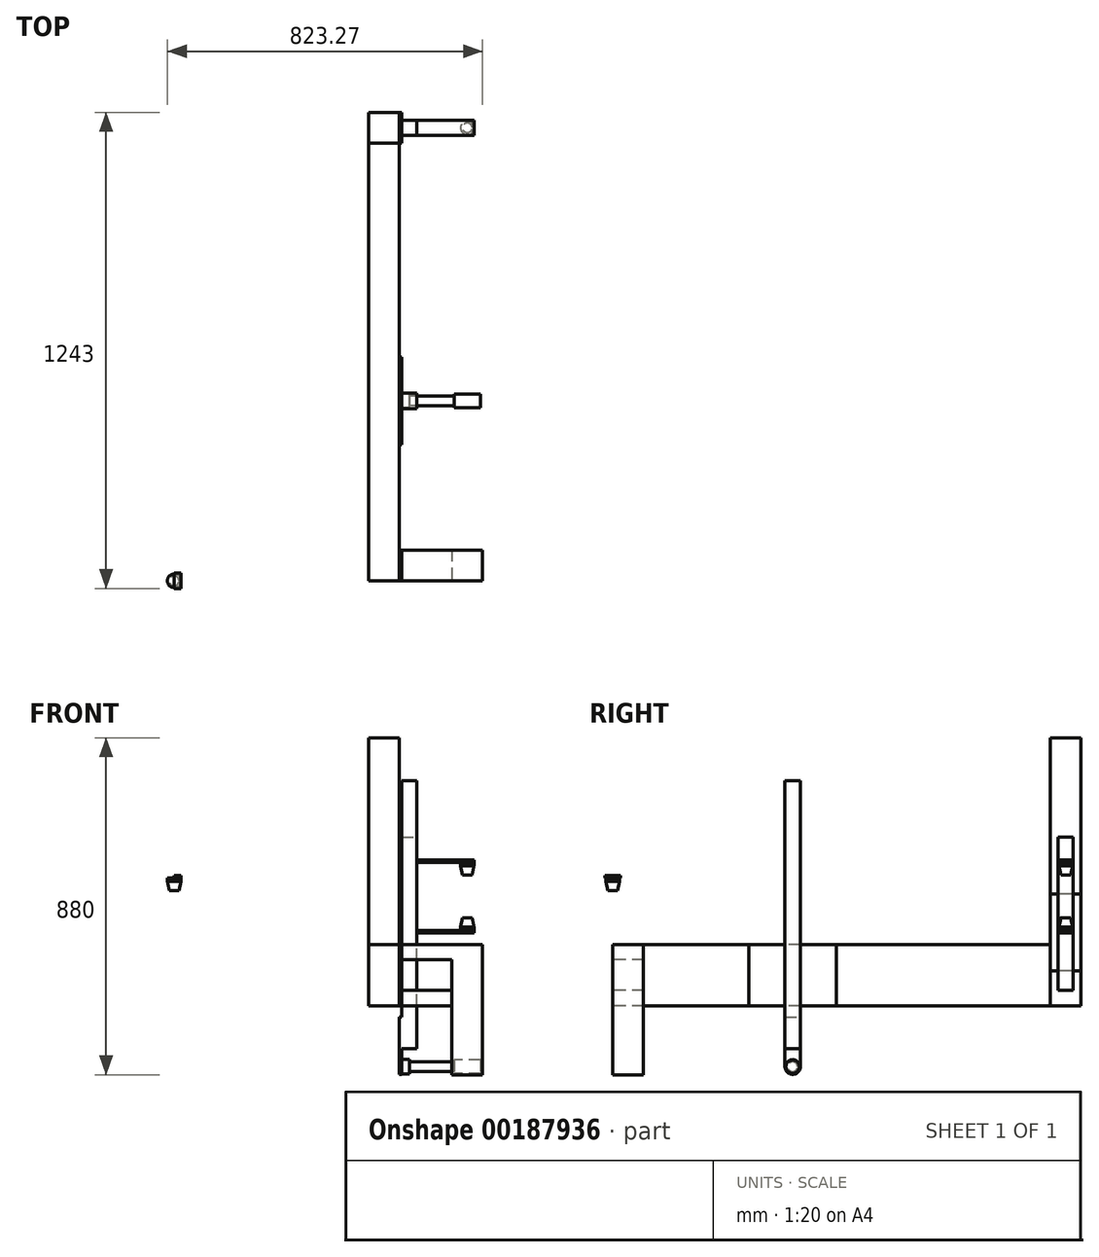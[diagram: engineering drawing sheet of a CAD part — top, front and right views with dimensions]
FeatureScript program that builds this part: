
annotation { "Feature Type Name" : "Feature", "Feature Type Description" : "" }
export const myFeature = defineFeature(function(context is Context, id is Id, definition is map)
    precondition{}
    {
        {
            var Q0;
            Q0=qCreatedBy(makeId("Front.planeOp"),FACE);
            var sketch = newSketch(context, id + "F0", { "sketchPlane" : qUnion([Q0])});
            skLineSegment(sketch, "E0", {"start": v(-374.77, -348.44) * mm, "end": v(-374.77, 351.56) * mm});
            skLineSegment(sketch, "E1", {"start": v(-334.77, -348.44) * mm, "end": v(-334.77, 351.56) * mm});
            skLineSegment(sketch, "E2", {"start": v(-334.77, 351.56) * mm, "end": v(-374.77, 351.56) * mm});
            skLineSegment(sketch, "E3", {"start": v(-334.77, -348.44) * mm, "end": v(-374.77, -348.44) * mm});
            skLineSegment(sketch, "E4", {"start": v(-374.77, -376.34) * mm, "end": v(-374.77, -413.47) * mm});
            skLineSegment(sketch, "E5", {"start": v(-374.77, -413.47) * mm, "end": v(-354.77, -413.47) * mm});
            skLineSegment(sketch, "E6", {"start": v(-354.77, -376.34) * mm, "end": v(-374.77, -376.34) * mm});
            skLineSegment(sketch, "E7", {"start": v(-381.12, -414.9) * mm, "end": v(-381.12, -264.9) * mm});
            skLineSegment(sketch, "E8", {"start": v(-381.12, -414.9) * mm, "end": v(-374.77, -414.9) * mm});
            skLineSegment(sketch, "E9", {"start": v(-374.77, -414.9) * mm, "end": v(-374.77, -264.9) * mm});
            skLineSegment(sketch, "E10", {"start": v(-374.77, -264.9) * mm, "end": v(-381.12, -264.9) * mm});
            skLineSegment(sketch, "E11.bottom", {"start": v(304.53, -11.1) * mm, "end": v(384.53, -11.1) * mm});
            skLineSegment(sketch, "E11.top", {"start": v(304.53, -171.1) * mm, "end": v(384.53, -171.1) * mm});
            skLineSegment(sketch, "E11.left", {"start": v(304.53, -11.1) * mm, "end": v(304.53, -171.1) * mm});
            skLineSegment(sketch, "E11.right", {"start": v(384.53, -11.1) * mm, "end": v(384.53, -171.1) * mm});
            skLineSegment(sketch, "E12", {"start": v(390.88, -11.1) * mm, "end": v(390.88, -171.1) * mm});
            skPoint(sketch, "E12.startSnap0", {"position": v(344.53, -11.1) * mm});
            skLineSegment(sketch, "E13", {"start": v(384.53, -11.1) * mm, "end": v(390.88, -11.1) * mm});
            skLineSegment(sketch, "E14", {"start": v(390.88, -11.1) * mm, "end": v(595.98, -11.1) * mm});
            skLineSegment(sketch, "E15", {"start": v(595.98, -11.1) * mm, "end": v(602.33, -11.1) * mm});
            skLineSegment(sketch, "E16", {"start": v(602.33, -11.1) * mm, "end": v(602.33, -51.1) * mm});
            skLineSegment(sketch, "E17", {"start": v(602.33, -51.1) * mm, "end": v(595.98, -51.1) * mm});
            skLineSegment(sketch, "E18", {"start": v(595.98, -51.1) * mm, "end": v(595.98, -11.1) * mm});
            skLineSegment(sketch, "E19", {"start": v(595.98, -51.1) * mm, "end": v(390.88, -51.1) * mm});
            skLineSegment(sketch, "E20", {"start": v(602.33, -51.1) * mm, "end": v(602.33, -351.1) * mm});
            skLineSegment(sketch, "E21", {"start": v(602.33, -351.1) * mm, "end": v(522.33, -351.1) * mm});
            skLineSegment(sketch, "E22", {"start": v(522.33, -351.1) * mm, "end": v(522.33, -51.1) * mm});
            skLineSegment(sketch, "E23", {"start": v(384.53, -171.1) * mm, "end": v(390.88, -171.1) * mm});
            skLineSegment(sketch, "E24", {"start": v(522.33, -171.1) * mm, "end": v(390.88, -171.1) * mm});
            skLineSegment(sketch, "E25", {"start": v(522.33, -171.1) * mm, "end": v(522.33, -131.1) * mm});
            skLineSegment(sketch, "E26", {"start": v(522.33, -131.1) * mm, "end": v(390.88, -131.1) * mm});
            skLineSegment(sketch, "E27", {"start": v(602.33, -222.88) * mm, "end": v(562.33, -222.88) * mm, "construction": true});
            skLineSegment(sketch, "E28", {"start": v(562.33, -222.88) * mm, "end": v(562.33, -101.4) * mm});
            skPoint(sketch, "E29", {"position": v(-381.12, -235.9) * mm});
            skLineSegment(sketch, "E30", {"start": v(-381.12, -235.9) * mm, "end": v(-381.12, -75.9) * mm});
            skLineSegment(sketch, "E31", {"start": v(-381.12, -75.9) * mm, "end": v(-374.77, -75.9) * mm});
            skLineSegment(sketch, "E32", {"start": v(-374.77, -75.9) * mm, "end": v(-374.77, -235.9) * mm});
            skLineSegment(sketch, "E33", {"start": v(-374.77, -235.9) * mm, "end": v(-381.12, -235.9) * mm});
            skLineSegment(sketch, "E34", {"start": v(-381.12, -394.9) * mm, "end": v(-203.32, -394.9) * mm});
            skLineSegment(sketch, "E35", {"start": v(-354.77, -376.34) * mm, "end": v(-354.77, -413.47) * mm});
            skLineSegment(sketch, "E36", {"start": v(-203.32, -394.9) * mm, "end": v(-203.32, 341.23) * mm});
            skLineSegment(sketch, "E37", {"start": v(-220.94, 162.85) * mm, "end": v(-203.32, 162.85) * mm});
            skLineSegment(sketch, "E38.MirrorCS", {"start": v(-185.7, 162.85) * mm, "end": v(-203.32, 162.85) * mm});
            skPoint(sketch, "E39", {"position": v(-203.32, 129.82) * mm});
            skPoint(sketch, "E40", {"position": v(-215.94, 129.82) * mm});
            skLineSegment(sketch, "E41", {"start": v(-220.94, 162.85) * mm, "end": v(-220.94, 153.82) * mm});
            skLineSegment(sketch, "E42", {"start": v(-220.94, 153.82) * mm, "end": v(-185.7, 153.82) * mm});
            skLineSegment(sketch, "E43", {"start": v(-185.7, 153.82) * mm, "end": v(-185.7, 162.85) * mm});
            skLineSegment(sketch, "E44", {"start": v(-220.94, 153.82) * mm, "end": v(-215.94, 129.82) * mm});
            skLineSegment(sketch, "E45", {"start": v(-203.32, 129.82) * mm, "end": v(-215.94, 129.82) * mm});
            skLineSegment(sketch, "E46.MirrorCS", {"start": v(-185.7, 153.82) * mm, "end": v(-190.7, 129.82) * mm});
            skLineSegment(sketch, "E47.MirrorCS", {"start": v(-203.32, 129.82) * mm, "end": v(-190.7, 129.82) * mm});
            skLineSegment(sketch, "E48", {"start": v(-185.7, 162.85) * mm, "end": v(-185.7, 169.2) * mm});
            skLineSegment(sketch, "E49", {"start": v(-185.7, 169.2) * mm, "end": v(-334.77, 169.2) * mm});
            skLineSegment(sketch, "E50", {"start": v(-334.77, 169.2) * mm, "end": v(-334.77, 162.85) * mm});
            skLineSegment(sketch, "E51", {"start": v(-334.77, 162.85) * mm, "end": v(-185.7, 162.85) * mm});
            skPoint(sketch, "E52", {"position": v(-237.32, -377.4) * mm});
            skLineSegment(sketch, "E53", {"start": v(-237.32, -377.4) * mm, "end": v(-203.32, -377.4) * mm});
            skLineSegment(sketch, "E54", {"start": v(-237.32, -377.4) * mm, "end": v(-237.32, -394.9) * mm});
            skLineSegment(sketch, "E55.MirrorCS", {"start": v(-237.32, -412.4) * mm, "end": v(-203.32, -412.4) * mm});
            skLineSegment(sketch, "E56.MirrorCS", {"start": v(-237.32, -412.4) * mm, "end": v(-237.32, -394.9) * mm});
            skLineSegment(sketch, "E57.MirrorCS", {"start": v(-169.32, -377.4) * mm, "end": v(-203.32, -377.4) * mm});
            skLineSegment(sketch, "E58.MirrorCS", {"start": v(-169.32, -377.4) * mm, "end": v(-169.32, -394.9) * mm});
            skLineSegment(sketch, "E59.MirrorCS", {"start": v(-25.52, -394.9) * mm, "end": v(-203.32, -394.9) * mm});
            skLineSegment(sketch, "E60.MirrorCS", {"start": v(-169.32, -412.4) * mm, "end": v(-203.32, -412.4) * mm});
            skLineSegment(sketch, "E61.MirrorCS", {"start": v(-169.32, -412.4) * mm, "end": v(-169.32, -394.9) * mm});
            skPoint(sketch, "E62", {"position": v(-354.77, -382.2) * mm});
            skPoint(sketch, "E63", {"position": v(-354.77, -394.9) * mm});
            skLineSegment(sketch, "E64", {"start": v(-354.77, -382.2) * mm, "end": v(-237.32, -382.2) * mm});
            skLineSegment(sketch, "E65.MirrorCS", {"start": v(-354.77, -407.6) * mm, "end": v(-237.32, -407.6) * mm});
            skPoint(sketch, "E66", {"position": v(-374.77, -394.9) * mm});
            skLineSegment(sketch, "E67", {"start": v(1447.18, -161.35) * mm, "end": v(1447.18, 38.65) * mm});
            skLineSegment(sketch, "E68", {"start": v(1447.18, 38.65) * mm, "end": v(1527.18, 38.65) * mm});
            skLineSegment(sketch, "E69", {"start": v(1527.18, 38.65) * mm, "end": v(1527.18, -161.35) * mm});
            skLineSegment(sketch, "E70", {"start": v(1447.18, -161.35) * mm, "end": v(1527.18, -161.35) * mm});
            skCircle(sketch, "E71", {"center": v(1507.18, 18.65) * mm, "radius": 4 * mm});
            skCircle(sketch, "E72", {"center": v(1467.18, -141.35) * mm, "radius": 4 * mm});
            skLineSegment(sketch, "E73", {"start": v(1496.49, 18.47) * mm, "end": v(1494.06, 30.94) * mm});
            skLineSegment(sketch, "E74", {"start": v(1493.7, 18.25) * mm, "end": v(1491.06, 30.68) * mm});
            skLineSegment(sketch, "E75", {"start": v(1490.91, 18) * mm, "end": v(1488.06, 30.38) * mm});
            skLineSegment(sketch, "E76", {"start": v(1488.14, 17.69) * mm, "end": v(1485.06, 30.02) * mm});
            skLineSegment(sketch, "E77", {"start": v(1486.65, 12.52) * mm, "end": v(1482.05, 29.7) * mm});
            skLineSegment(sketch, "E78", {"start": v(1482.6, 16.93) * mm, "end": v(1479.1, 29.14) * mm});
            skLineSegment(sketch, "E79", {"start": v(1479.84, 16.47) * mm, "end": v(1476.12, 28.62) * mm});
            skLineSegment(sketch, "E80", {"start": v(1477.09, 15.97) * mm, "end": v(1473.16, 28.06) * mm});
            skLineSegment(sketch, "E81", {"start": v(1474.35, 15.42) * mm, "end": v(1470.21, 27.44) * mm});
            skLineSegment(sketch, "E82", {"start": v(1473.32, 10.15) * mm, "end": v(1467.24, 26.85) * mm});
            skLineSegment(sketch, "E83", {"start": v(1468.9, 14.18) * mm, "end": v(1464.34, 26.04) * mm});
            skLineSegment(sketch, "E84", {"start": v(1466.19, 13.49) * mm, "end": v(1461.43, 25.27) * mm});
            skLineSegment(sketch, "E85", {"start": v(1463.5, 12.75) * mm, "end": v(1458.53, 24.45) * mm});
            skLineSegment(sketch, "E86", {"start": v(1460.81, 11.96) * mm, "end": v(1455.64, 23.57) * mm});
            skLineSegment(sketch, "E87", {"start": v(1460.25, 6.62) * mm, "end": v(1452.73, 22.73) * mm});
            skCircle(sketch, "E88", {"center": v(1518.58, -38.02) * mm, "radius": 3.37 * mm});
            skCircle(sketch, "E89", {"center": v(1507.18, -141.35) * mm, "radius": 4 * mm});
            skCircle(sketch, "E90", {"center": v(1507.18, 3.65) * mm, "radius": 3.96 * mm});
            skCircle(sketch, "E91", {"center": v(1467.18, -126.35) * mm, "radius": 3.96 * mm});
            skCircle(sketch, "E92", {"center": v(1507.18, -126.35) * mm, "radius": 3.96 * mm});
            skLineSegment(sketch, "E93", {"start": v(1416.45, 134) * mm, "end": v(1403.21, 209.03) * mm});
            skLineSegment(sketch, "E94", {"start": v(1403.21, 209.03) * mm, "end": v(1445.73, 216.53) * mm});
            skLineSegment(sketch, "E95", {"start": v(1416.45, 134) * mm, "end": v(1458.96, 141.49) * mm});
            skLineSegment(sketch, "E96", {"start": v(1445.73, 216.53) * mm, "end": v(1458.96, 141.49) * mm});
            skArc(sketch, "E97", {"start": v(1442.98, 167.35) * mm, "mid": v(1430.51, 171.3) * mm, "end": v(1417.64, 173.58) * mm});
            skArc(sketch, "E98", {"start": v(1445.88, 174.8) * mm, "mid": v(1432.42, 179.06) * mm, "end": v(1418.52, 181.53) * mm});
            skArc(sketch, "E99", {"start": v(1418.52, 181.53) * mm, "mid": v(1414.1, 178) * mm, "end": v(1417.64, 173.58) * mm});
            skArc(sketch, "E100", {"start": v(1442.98, 167.35) * mm, "mid": v(1448.16, 169.63) * mm, "end": v(1445.88, 174.8) * mm});
            skLineSegment(sketch, "E101.bottom", {"start": v(897.87, 19.19) * mm, "end": v(904.22, 19.19) * mm});
            skLineSegment(sketch, "E101.top", {"start": v(897.87, -180.81) * mm, "end": v(904.22, -180.81) * mm});
            skLineSegment(sketch, "E101.left", {"start": v(897.87, 19.19) * mm, "end": v(897.87, -180.81) * mm});
            skLineSegment(sketch, "E101.right", {"start": v(904.22, 19.19) * mm, "end": v(904.22, -180.81) * mm});
            skLineSegment(sketch, "E102", {"start": v(944.22, -232.06) * mm, "end": v(944.22, 167.94) * mm});
            skLineSegment(sketch, "E103", {"start": v(904.22, 19.19) * mm, "end": v(904.22, 167.94) * mm});
            skLineSegment(sketch, "E104", {"start": v(904.22, 167.94) * mm, "end": v(944.22, 167.94) * mm});
            skLineSegment(sketch, "E105", {"start": v(904.22, -180.81) * mm, "end": v(904.22, -232.06) * mm});
            skLineSegment(sketch, "E106", {"start": v(904.22, -232.06) * mm, "end": v(944.22, -232.06) * mm});
            skLineSegment(sketch, "E107", {"start": v(1075.67, 222.27) * mm, "end": v(1075.67, -239.92) * mm, "construction": true});
            skLineSegment(sketch, "E108", {"start": v(842.92, 393.35) * mm, "end": v(842.92, 384.33) * mm});
            skLineSegment(sketch, "E109", {"start": v(842.92, 384.33) * mm, "end": v(878.17, 384.33) * mm});
            skLineSegment(sketch, "E110", {"start": v(878.17, 384.33) * mm, "end": v(878.17, 393.35) * mm});
            skLineSegment(sketch, "E111", {"start": v(842.92, 384.33) * mm, "end": v(847.92, 360.33) * mm});
            skLineSegment(sketch, "E112", {"start": v(860.54, 360.33) * mm, "end": v(847.92, 360.33) * mm});
            skLineSegment(sketch, "E113.MirrorCS", {"start": v(878.17, 384.33) * mm, "end": v(873.17, 360.33) * mm});
            skLineSegment(sketch, "E114.MirrorCS", {"start": v(860.54, 360.33) * mm, "end": v(873.17, 360.33) * mm});
            skLineSegment(sketch, "E115", {"start": v(2139.53, 452.77) * mm, "end": v(2139.53, -9.42) * mm, "construction": true});
            skLineSegment(sketch, "E116", {"start": v(860.54, 360.33) * mm, "end": v(860.54, 393.35) * mm});
            skLineSegment(sketch, "E117", {"start": v(1075.67, 123.78) * mm, "end": v(1093.3, 123.78) * mm, "construction": true});
            skLineSegment(sketch, "E118", {"start": v(944.22, 109.05) * mm, "end": v(1093.3, 109.05) * mm});
            skLineSegment(sketch, "E119", {"start": v(1093.3, 109.05) * mm, "end": v(1093.3, 102.7) * mm});
            skLineSegment(sketch, "E120", {"start": v(1093.3, 102.7) * mm, "end": v(944.22, 102.7) * mm});
            skLineSegment(sketch, "E121.MirrorCS", {"start": v(1075.67, 123.78) * mm, "end": v(1058.05, 123.78) * mm, "construction": true});
            skLineSegment(sketch, "E122", {"start": v(1058.05, 102.7) * mm, "end": v(1058.05, 93.8) * mm});
            skLineSegment(sketch, "E123", {"start": v(1058.05, 93.8) * mm, "end": v(1075.67, 93.8) * mm});
            skLineSegment(sketch, "E124.MirrorCS", {"start": v(1075.67, 69.68) * mm, "end": v(1063.05, 69.68) * mm});
            skLineSegment(sketch, "E125", {"start": v(1058.05, 93.8) * mm, "end": v(1063.05, 69.68) * mm});
            skPoint(sketch, "E126", {"position": v(1075.67, 13.8) * mm});
            skLineSegment(sketch, "E127", {"start": v(1060.15, 13.8) * mm, "end": v(1101.33, 13.8) * mm, "construction": true});
            skLineSegment(sketch, "E128.MirrorCS", {"start": v(944.22, -81.43) * mm, "end": v(1093.3, -81.43) * mm});
            skLineSegment(sketch, "E129.MirrorCS", {"start": v(1093.3, -75.08) * mm, "end": v(944.22, -75.08) * mm});
            skLineSegment(sketch, "E130.MirrorCS", {"start": v(1075.67, -42.06) * mm, "end": v(1063.05, -42.06) * mm});
            skLineSegment(sketch, "E131.MirrorCS", {"start": v(1058.05, -66.2) * mm, "end": v(1063.05, -42.06) * mm});
            skLineSegment(sketch, "E132.MirrorCS", {"start": v(1058.05, -75.08) * mm, "end": v(1058.05, -66.2) * mm});
            skLineSegment(sketch, "E133.MirrorCS", {"start": v(1093.3, -81.43) * mm, "end": v(1093.3, -75.08) * mm});
            skLineSegment(sketch, "E134", {"start": v(1075.67, 102.7) * mm, "end": v(1075.67, 69.68) * mm});
            skLineSegment(sketch, "E135", {"start": v(1075.67, -42.06) * mm, "end": v(1075.67, -75.08) * mm});
            skPoint(sketch, "E136.orphan", {"position": v(1093.3, 93.8) * mm});
            skLineSegment(sketch, "E137", {"start": v(1058.05, -66.2) * mm, "end": v(1075.67, -66.2) * mm});
            skSolve(sketch);
        }
        {
            var Q0;
            Q0=makeQuery(id+"F0.imprint","IMPRINT",FACE,{"disambiguationData":[TD([[makeQuery(id+"F0.imprint","IMPRINT",EDGE,{"derivedFrom":sQuery(id+"F0.wireOp",EDGE,"E11.bottom")}),-1.0]])]});
            extrude(context, id + "F1", {"entities" : qUnion([Q0]), "oppositeDirection" : true, "depth" : 1143 * mm});
        }
        {
            var Q0;
            {var subQ3=sQuery(id+"F0.wireOp",EDGE,"E14");Q0=makeQuery(id+"F0.imprint","IMPRINT",FACE,{"disambiguationData":[TD([[makeQuery(id+"F0.imprint","IMPRINT",EDGE,{"derivedFrom":subQ3}),-1.0]])]});}
            extrude(context, id + "F2", {"entities" : qUnion([Q0]), "oppositeDirection" : true, "depth" : 80 * mm});
        }
        {
            var Q0;
            {var subQ1=sQuery(id+"F0.wireOp",EDGE,"E17");Q0=makeQuery(id+"F0.imprint","IMPRINT",FACE,{"disambiguationData":[TD([[makeQuery(id+"F0.imprint","IMPRINT",EDGE,{"derivedFrom":subQ1}),1.0]])]});}
            extrude(context, id + "F3", {"entities" : qUnion([Q0]), "operationType" : NewBodyOperationType.ADD, "oppositeDirection" : true, "depth" : 80 * mm});
        }
        {
            var Q0;
            Q0=makeQuery(id+"F0.imprint","IMPRINT",FACE,{"disambiguationData":[TD([[makeQuery(id+"F0.imprint","IMPRINT",EDGE,{"derivedFrom":sQuery(id+"F0.wireOp",EDGE,"E15")}),-1.0]])]});
            extrude(context, id + "F4", {"entities" : qUnion([Q0]), "operationType" : NewBodyOperationType.ADD, "oppositeDirection" : true, "depth" : 80 * mm});
        }
        {
            var Q0;
            Q0=makeQuery(id+"F0.imprint","IMPRINT",FACE,{"disambiguationData":[TD([[makeQuery(id+"F0.imprint","IMPRINT",EDGE,{"derivedFrom":sQuery(id+"F0.wireOp",EDGE,"E11.right")}),1.0]])]});
            extrude(context, id + "F5", {"entities" : qUnion([Q0]), "oppositeDirection" : true, "depth" : 80 * mm});
        }
        {
            var Q0;
            Q0=makeQuery(id+"F1.opExtrude","SWEPT_FACE",FACE,{"disambiguationData":[OSD([sQuery(id+"F0.wireOp",EDGE,"E11.right")])]});
            extrude(context, id + "F6", {"entities" : qUnion([Q0]), "oppositeDirection" : true, "depth" : 80 * mm});
        }
        {
            var Q0;
            Q0=makeQuery(id+"F1.opExtrude","CAP_FACE",FACE,{"disambiguationData":[OSD([sQuery(id+"F0.wireOp",EDGE,"E11.bottom"),sQuery(id+"F0.wireOp",EDGE,"E11.top"),sQuery(id+"F0.wireOp",EDGE,"E11.left"),sQuery(id+"F0.wireOp",EDGE,"E11.right")])],"isStart":false});
            var sketch = newSketch(context, id + "F7", { "sketchPlane" : qUnion([Q0])});
            skLineSegment(sketch, "E138.bottom", {"start": v(-384.53, -171.1) * mm, "end": v(-304.53, -171.1) * mm});
            skLineSegment(sketch, "E138.top", {"start": v(-384.53, -171.1) * mm, "end": v(-304.53, -171.1) * mm});
            skLineSegment(sketch, "E138.left", {"start": v(-384.53, -171.1) * mm, "end": v(-384.53, -171.1) * mm});
            skLineSegment(sketch, "E138.right", {"start": v(-304.53, -171.1) * mm, "end": v(-304.53, -171.1) * mm});
            skLineSegment(sketch, "E139.bottom", {"start": v(-304.53, 528.9) * mm, "end": v(-384.53, 528.9) * mm});
            skLineSegment(sketch, "E139.top", {"start": v(-304.53, -171.1) * mm, "end": v(-384.53, -171.1) * mm});
            skLineSegment(sketch, "E139.left", {"start": v(-304.53, 528.9) * mm, "end": v(-304.53, -171.1) * mm});
            skLineSegment(sketch, "E139.right", {"start": v(-384.53, 528.9) * mm, "end": v(-384.53, -171.1) * mm});
            skSolve(sketch);
        }
        {
            var Q0;
            Q0 = qSketchRegion(id + "F7", true);
            extrude(context, id + "F8", {"entities" : qUnion([Q0]), "depth" : 80 * mm});
        }
        {
            var Q0;
            {var subQ0=sQuery(id+"F0.wireOp",EDGE,"E24");Q0=makeQuery(id+"F0.imprint","IMPRINT",FACE,{"disambiguationData":[TD([[makeQuery(id+"F0.imprint","IMPRINT",EDGE,{"derivedFrom":subQ0}),-1.0]])]});}
            extrude(context, id + "F9", {"entities" : qUnion([Q0]), "oppositeDirection" : true, "depth" : 80 * mm});
        }
        {
            var Q0;
            {var subQ0=sQuery(id+"F0.wireOp",EDGE,"E2");Q0=makeQuery(id+"F0.imprint","IMPRINT",FACE,{"disambiguationData":[TD([[makeQuery(id+"F0.imprint","IMPRINT",EDGE,{"derivedFrom":subQ0}),1.0]])]});}
            var Q1;
            Q1=sQuery(id+"F0.wireOp",EDGE,"E34");
            var Q2;
            Q2=sQuery(id+"F0.wireOp",EDGE,"E59.MirrorCS");
            extrude(context, id + "F10", {"entities" : qUnion([Q0]), "surfaceEntities" : qUnion([Q1, Q2]), "endBound" : BoundingType.SYMMETRIC, "oppositeDirection" : true, "depth" : 40 * mm});
        }
        {
            var Q0;
            {var subQ5=sQuery(id+"F0.wireOp",EDGE,"E64");Q0=makeQuery(id+"F0.imprint","IMPRINT",FACE,{"disambiguationData":[TD([[makeQuery(id+"F0.imprint","IMPRINT",EDGE,{"derivedFrom":subQ5}),-1.0]])]});}
            var Q1;
            Q1=sQuery(id+"F0.wireOp",EDGE,"E34");
            revolve(context, id + "F11", {"entities" : qUnion([Q0]), "axis" : qUnion([Q1]), "revolveType" : RevolveType.FULL});
        }
        {
            var Q0;
            Q0=makeQuery(id+"F0.imprint","IMPRINT",FACE,{"disambiguationData":[TD([[makeQuery(id+"F0.imprint","IMPRINT",EDGE,{"derivedFrom":sQuery(id+"F0.wireOp",EDGE,"E30")}),-1.0]])]});
            extrude(context, id + "F12", {"entities" : qUnion([Q0]), "operationType" : NewBodyOperationType.ADD, "endBound" : BoundingType.SYMMETRIC, "oppositeDirection" : true, "depth" : 228.6 * mm});
        }
        {
            var Q0;
            {var subQ7=sQuery(id+"F0.wireOp",EDGE,"E10");Q0=makeQuery(id+"F0.imprint","IMPRINT",FACE,{"disambiguationData":[TD([[makeQuery(id+"F0.imprint","IMPRINT",EDGE,{"derivedFrom":subQ7}),1.0]])]});}
            var Q1;
            {var subQ4=sQuery(id+"F0.wireOp",EDGE,"E8");Q1=makeQuery(id+"F0.imprint","IMPRINT",FACE,{"disambiguationData":[TD([[makeQuery(id+"F0.imprint","IMPRINT",EDGE,{"derivedFrom":subQ4}),1.0]])]});}
            extrude(context, id + "F13", {"entities" : qUnion([Q0, Q1]), "operationType" : NewBodyOperationType.ADD, "endBound" : BoundingType.SYMMETRIC, "depth" : 40 * mm});
        }
        {
            var Q0;
            Q0=makeQuery(id+"F13.opExtrude","CAP_EDGE",EDGE,{"disambiguationData":[OSD([sQuery(id+"F0.wireOp",EDGE,"E8")])],"isStart":false});
            var Q1;
            Q1=makeQuery(id+"F13.opExtrude","CAP_EDGE",EDGE,{"disambiguationData":[OSD([sQuery(id+"F0.wireOp",EDGE,"E8")])],"isStart":true});
            fillet(context, id + "F14", {"entities" : qUnion([Q0, Q1]), "radius" : 20 * mm, "tangentPropagation" : true, "allowEdgeOverflow" : false});
        }
        {
            var Q0;
            {var subQ5=sQuery(id+"F0.wireOp",EDGE,"E6");Q0=makeQuery(id+"F0.imprint","IMPRINT",FACE,{"disambiguationData":[TD([[makeQuery(id+"F0.imprint","IMPRINT",EDGE,{"derivedFrom":subQ5}),1.0]])]});}
            var Q1;
            Q1=sQuery(id+"F0.wireOp",EDGE,"E34");
            revolve(context, id + "F15", {"entities" : qUnion([Q0]), "axis" : qUnion([Q1]), "revolveType" : RevolveType.FULL});
        }
        {
            var Q0;
            {var subQ1=sQuery(id+"F0.wireOp",EDGE,"E53");Q0=makeQuery(id+"F0.imprint","IMPRINT",FACE,{"disambiguationData":[TD([[makeQuery(id+"F0.imprint","IMPRINT",EDGE,{"derivedFrom":subQ1}),-1.0]])]});}
            var Q1;
            {var subQ3=sQuery(id+"F0.wireOp",EDGE,"E57.MirrorCS");Q1=makeQuery(id+"F0.imprint","IMPRINT",FACE,{"disambiguationData":[TD([[makeQuery(id+"F0.imprint","IMPRINT",EDGE,{"derivedFrom":subQ3}),1.0]])]});}
            var Q2;
            Q2=sQuery(id+"F0.wireOp",EDGE,"E53");
            var Q3;
            Q3=sQuery(id+"F0.wireOp",EDGE,"E57.MirrorCS");
            var Q4;
            Q4=sQuery(id+"F0.wireOp",EDGE,"E34");
            revolve(context, id + "F16", {"operationType" : NewBodyOperationType.ADD, "entities" : qUnion([Q0, Q1]), "surfaceEntities" : qUnion([Q2, Q3]), "axis" : qUnion([Q4]), "revolveType" : RevolveType.FULL});
        }
        {
            var Q0;
            {var subQ2=sQuery(id+"F0.wireOp",EDGE,"E50");Q0=makeQuery(id+"F0.imprint","IMPRINT",FACE,{"disambiguationData":[TD([[makeQuery(id+"F0.imprint","IMPRINT",EDGE,{"derivedFrom":subQ2}),1.0]])]});}
            var Q1;
            {var subQ5=sQuery(id+"F0.wireOp",EDGE,"E48");Q1=makeQuery(id+"F0.imprint","IMPRINT",FACE,{"disambiguationData":[TD([[makeQuery(id+"F0.imprint","IMPRINT",EDGE,{"derivedFrom":subQ5}),1.0]])]});}
            var Q2;
            Q2=sQuery(id+"F0.wireOp",EDGE,"E49");
            extrude(context, id + "F17", {"entities" : qUnion([Q0, Q1]), "operationType" : NewBodyOperationType.ADD, "surfaceEntities" : qUnion([Q2]), "endBound" : BoundingType.SYMMETRIC, "depth" : 40 * mm});
        }
        {
            var Q0;
            {var subQ5=sQuery(id+"F0.wireOp",EDGE,"E41");Q0=makeQuery(id+"F0.imprint","IMPRINT",FACE,{"disambiguationData":[TD([[makeQuery(id+"F0.imprint","IMPRINT",EDGE,{"derivedFrom":subQ5}),1.0]])]});}
            var Q1;
            {var subQ4=sQuery(id+"F0.wireOp",EDGE,"E44");Q1=makeQuery(id+"F0.imprint","IMPRINT",FACE,{"disambiguationData":[TD([[makeQuery(id+"F0.imprint","IMPRINT",EDGE,{"derivedFrom":subQ4}),1.0]])]});}
            var Q2;
            Q2=sQuery(id+"F0.wireOp",EDGE,"E36");
            revolve(context, id + "F18", {"operationType" : NewBodyOperationType.ADD, "entities" : qUnion([Q0, Q1]), "axis" : qUnion([Q2]), "revolveType" : RevolveType.FULL});
        }
        {
            var Q0;
            Q0=makeQuery(id+"F15.opRevolve","SWEPT_BODY",BODY,{"disambiguationData":[OSD([sQuery(id+"F0.wireOp",EDGE,"E6"),sQuery(id+"F0.wireOp",EDGE,"E9"),sQuery(id+"F0.wireOp",EDGE,"E34"),sQuery(id+"F0.wireOp",EDGE,"E35")])]});
            var Q1;
            Q1=makeQuery(id+"F10.opExtrude","SWEPT_BODY",BODY,{"disambiguationData":[OSD([sQuery(id+"F0.wireOp",EDGE,"E0"),sQuery(id+"F0.wireOp",EDGE,"E1"),sQuery(id+"F0.wireOp",EDGE,"E2"),sQuery(id+"F0.wireOp",EDGE,"E3"),sQuery(id+"F0.wireOp",EDGE,"E9"),sQuery(id+"F0.wireOp",EDGE,"E32"),sQuery(id+"F0.wireOp",EDGE,"E50")])]});
            var Q2;
            Q2=makeQuery(id+"F11.opRevolve","SWEPT_BODY",BODY,{"disambiguationData":[OSD([sQuery(id+"F0.wireOp",EDGE,"E34"),sQuery(id+"F0.wireOp",EDGE,"E35"),sQuery(id+"F0.wireOp",EDGE,"E54"),sQuery(id+"F0.wireOp",EDGE,"E64")])]});
            var Q3;
            Q3=makeQuery(id+"F12.opExtrude","CAP_VERTEX",VERTEX,{"disambiguationData":[OSD([sQuery(id+"F0.wireOp",EDGE,"E30"),sQuery(id+"F0.wireOp",EDGE,"E31")])],"isStart":false});
            var Q4;
            Q4=makeQuery(id+"F1.opExtrude","CAP_VERTEX",VERTEX,{"disambiguationData":[OSD([sQuery(id+"F0.wireOp",EDGE,"E11.bottom"),sQuery(id+"F0.wireOp",EDGE,"E11.right"),sQuery(id+"F0.wireOp",EDGE,"E13")])],"isStart":false});
            transform(context, id + "F19", {"entities" : qUnion([Q0, Q1, Q2]), "transformType" : TransformType.TRANSLATION_ENTITY, "oppositeDirectionEntity" : false, "transformLine" : qUnion([Q3, Q4]), "makeCopy" : false});
        }
        {
            var Q0;
            Q0=makeQuery(id+"F10.opExtrude","SWEPT_BODY",BODY,{"disambiguationData":[OSD([sQuery(id+"F0.wireOp",EDGE,"E0"),sQuery(id+"F0.wireOp",EDGE,"E1"),sQuery(id+"F0.wireOp",EDGE,"E2"),sQuery(id+"F0.wireOp",EDGE,"E3"),sQuery(id+"F0.wireOp",EDGE,"E9"),sQuery(id+"F0.wireOp",EDGE,"E32"),sQuery(id+"F0.wireOp",EDGE,"E50")])]});
            var Q1;
            Q1=makeQuery(id+"F11.opRevolve","SWEPT_BODY",BODY,{"disambiguationData":[OSD([sQuery(id+"F0.wireOp",EDGE,"E34"),sQuery(id+"F0.wireOp",EDGE,"E35"),sQuery(id+"F0.wireOp",EDGE,"E54"),sQuery(id+"F0.wireOp",EDGE,"E64")])]});
            var Q2;
            Q2=makeQuery(id+"F15.opRevolve","SWEPT_BODY",BODY,{"disambiguationData":[OSD([sQuery(id+"F0.wireOp",EDGE,"E6"),sQuery(id+"F0.wireOp",EDGE,"E9"),sQuery(id+"F0.wireOp",EDGE,"E34"),sQuery(id+"F0.wireOp",EDGE,"E35")])]});
            var Q3;
            Q3=makeQuery(id+"F1.opExtrude","SWEPT_EDGE",EDGE,{"disambiguationData":[OSD([sQuery(id+"F0.wireOp",EDGE,"E11.bottom"),sQuery(id+"F0.wireOp",EDGE,"E11.right"),sQuery(id+"F0.wireOp",EDGE,"E13")])]});
            var Q4;
            {var subQ0=sQuery(id+"F0.wireOp",EDGE,"E33");var subQ1=sQuery(id+"F0.wireOp",EDGE,"E32");var subQ2=sQuery(id+"F0.wireOp",EDGE,"E31");Q4=makeQuery(id+"F12.boolean.opBoolean","SPLIT",FACE,{"disambiguationData":[TD([makeQuery(id+"F12.opExtrude","CAP_FACE",FACE,{"disambiguationData":[OSD([sQuery(id+"F0.wireOp",EDGE,"E30"),subQ2,subQ1,subQ0])],"isStart":false})])],"derivedFrom":makeQuery(id+"F12.opExtrude","SWEPT_FACE",FACE,{"disambiguationData":[OSD([subQ1])]})});}
            transform(context, id + "F20", {"entities" : qUnion([Q0, Q1, Q2]), "transformType" : TransformType.TRANSLATION_DISTANCE, "transformDirection" : qUnion([Q3, Q4]), "distance" : 558.8 * mm, "makeCopy" : false});
        }
        {
            var Q0;
            Q0=makeQuery(id+"F0.imprint","IMPRINT",FACE,{"disambiguationData":[TD([[makeQuery(id+"F0.imprint","IMPRINT",EDGE,{"derivedFrom":sQuery(id+"F0.wireOp",EDGE,"E101.right")}),1.0]])]});
            var Q1;
            {var subQ3=sQuery(id+"F0.wireOp",EDGE,"E118");Q1=makeQuery(id+"F0.imprint","IMPRINT",FACE,{"disambiguationData":[TD([[makeQuery(id+"F0.imprint","IMPRINT",EDGE,{"derivedFrom":subQ3}),-1.0]])]});}
            var Q2;
            {var subQ4=sQuery(id+"F0.wireOp",EDGE,"E128.MirrorCS");Q2=makeQuery(id+"F0.imprint","IMPRINT",FACE,{"disambiguationData":[TD([[makeQuery(id+"F0.imprint","IMPRINT",EDGE,{"derivedFrom":subQ4}),1.0]])]});}
            extrude(context, id + "F21", {"entities" : qUnion([Q0, Q1, Q2]), "endBound" : BoundingType.SYMMETRIC, "oppositeDirection" : true, "depth" : 40 * mm});
        }
        {
            var Q0;
            Q0=makeQuery(id+"F0.imprint","IMPRINT",FACE,{"disambiguationData":[TD([[makeQuery(id+"F0.imprint","IMPRINT",EDGE,{"derivedFrom":sQuery(id+"F0.wireOp",EDGE,"E101.bottom")}),-1.0]])]});
            extrude(context, id + "F22", {"entities" : qUnion([Q0]), "operationType" : NewBodyOperationType.ADD, "endBound" : BoundingType.SYMMETRIC, "oppositeDirection" : true, "depth" : 80 * mm});
        }
        {
            var Q0;
            {var subQ0=sQuery(id+"F0.wireOp",EDGE,"E122");Q0=makeQuery(id+"F0.imprint","IMPRINT",FACE,{"disambiguationData":[TD([[makeQuery(id+"F0.imprint","IMPRINT",EDGE,{"derivedFrom":subQ0}),1.0]])]});}
            var Q1;
            {var subQ0=sQuery(id+"F0.wireOp",EDGE,"E123");Q1=makeQuery(id+"F0.imprint","IMPRINT",FACE,{"disambiguationData":[TD([[makeQuery(id+"F0.imprint","IMPRINT",EDGE,{"derivedFrom":subQ0}),-1.0]])]});}
            var Q2;
            {var subQ0=sQuery(id+"F0.wireOp",EDGE,"E130.MirrorCS");Q2=makeQuery(id+"F0.imprint","IMPRINT",FACE,{"disambiguationData":[TD([[makeQuery(id+"F0.imprint","IMPRINT",EDGE,{"derivedFrom":subQ0}),1.0]])]});}
            var Q3;
            {var subQ0=sQuery(id+"F0.wireOp",EDGE,"E132.MirrorCS");Q3=makeQuery(id+"F0.imprint","IMPRINT",FACE,{"disambiguationData":[TD([[makeQuery(id+"F0.imprint","IMPRINT",EDGE,{"derivedFrom":subQ0}),-1.0]])]});}
            var Q4;
            Q4=sQuery(id+"F0.wireOp",EDGE,"E107");
            revolve(context, id + "F23", {"operationType" : NewBodyOperationType.ADD, "entities" : qUnion([Q0, Q1, Q2, Q3]), "axis" : qUnion([Q4]), "revolveType" : RevolveType.FULL});
        }
        {
            var Q0;
            Q0=makeQuery(id+"F21.opExtrude","SWEPT_BODY",BODY,{"disambiguationData":[OSD([sQuery(id+"F0.wireOp",EDGE,"E101.right"),sQuery(id+"F0.wireOp",EDGE,"E102"),sQuery(id+"F0.wireOp",EDGE,"E103"),sQuery(id+"F0.wireOp",EDGE,"E104"),sQuery(id+"F0.wireOp",EDGE,"E105"),sQuery(id+"F0.wireOp",EDGE,"E106"),sQuery(id+"F0.wireOp",EDGE,"E118"),sQuery(id+"F0.wireOp",EDGE,"E119"),sQuery(id+"F0.wireOp",EDGE,"E120"),sQuery(id+"F0.wireOp",EDGE,"E128.MirrorCS"),sQuery(id+"F0.wireOp",EDGE,"E129.MirrorCS"),sQuery(id+"F0.wireOp",EDGE,"E133.MirrorCS")])]});
            var Q1;
            Q1=makeQuery(id+"F8.opExtrude","CAP_EDGE",EDGE,{"disambiguationData":[OSD([sQuery(id+"F7.wireOp",EDGE,"E139.right")])],"isStart":true});
            transform(context, id + "F24", {"entities" : qUnion([Q0]), "transformType" : TransformType.TRANSLATION_3D, "dx" : -474.73 * mm, "dy" : 1180.6 * mm, "dz" : 0 * mm, "makeCopy" : false});
        }
        {
            var Q0;
            Q0=makeQuery(id+"F21.opExtrude","SWEPT_BODY",BODY,{"disambiguationData":[OSD([sQuery(id+"F0.wireOp",EDGE,"E101.right"),sQuery(id+"F0.wireOp",EDGE,"E102"),sQuery(id+"F0.wireOp",EDGE,"E103"),sQuery(id+"F0.wireOp",EDGE,"E104"),sQuery(id+"F0.wireOp",EDGE,"E105"),sQuery(id+"F0.wireOp",EDGE,"E106"),sQuery(id+"F0.wireOp",EDGE,"E118"),sQuery(id+"F0.wireOp",EDGE,"E119"),sQuery(id+"F0.wireOp",EDGE,"E120"),sQuery(id+"F0.wireOp",EDGE,"E128.MirrorCS"),sQuery(id+"F0.wireOp",EDGE,"E129.MirrorCS"),sQuery(id+"F0.wireOp",EDGE,"E133.MirrorCS")])]});
            transform(context, id + "F25", {"entities" : qUnion([Q0]), "transformType" : TransformType.TRANSLATION_3D, "dx" : -35.56 * mm, "dy" : 2.54 * mm, "dz" : 0 * mm, "makeCopy" : false});
        }
        {
            var Q0;
            Q0=makeQuery(id+"F21.opExtrude","SWEPT_BODY",BODY,{"disambiguationData":[OSD([sQuery(id+"F0.wireOp",EDGE,"E101.right"),sQuery(id+"F0.wireOp",EDGE,"E102"),sQuery(id+"F0.wireOp",EDGE,"E103"),sQuery(id+"F0.wireOp",EDGE,"E104"),sQuery(id+"F0.wireOp",EDGE,"E105"),sQuery(id+"F0.wireOp",EDGE,"E106"),sQuery(id+"F0.wireOp",EDGE,"E118"),sQuery(id+"F0.wireOp",EDGE,"E119"),sQuery(id+"F0.wireOp",EDGE,"E120"),sQuery(id+"F0.wireOp",EDGE,"E128.MirrorCS"),sQuery(id+"F0.wireOp",EDGE,"E129.MirrorCS"),sQuery(id+"F0.wireOp",EDGE,"E133.MirrorCS")])]});
            var Q1;
            Q1=makeQuery(id+"F22.opExtrude","CAP_VERTEX",VERTEX,{"disambiguationData":[OSD([sQuery(id+"F0.wireOp",EDGE,"E101.top"),sQuery(id+"F0.wireOp",EDGE,"E101.left")])],"isStart":true});
            var Q2;
            Q2=makeQuery(id+"F1.opExtrude","CAP_VERTEX",VERTEX,{"disambiguationData":[OSD([sQuery(id+"F0.wireOp",EDGE,"E11.top"),sQuery(id+"F0.wireOp",EDGE,"E11.right"),sQuery(id+"F0.wireOp",EDGE,"E23")])],"isStart":false});
            transform(context, id + "F26", {"entities" : qUnion([Q0]), "transformType" : TransformType.TRANSLATION_ENTITY, "oppositeDirectionEntity" : false, "transformLine" : qUnion([Q1, Q2]), "makeCopy" : false});
        }
        {
            var Q0;
            Q0=makeQuery(id+"F21.opExtrude","SWEPT_BODY",BODY,{"disambiguationData":[OSD([sQuery(id+"F0.wireOp",EDGE,"E101.right"),sQuery(id+"F0.wireOp",EDGE,"E102"),sQuery(id+"F0.wireOp",EDGE,"E103"),sQuery(id+"F0.wireOp",EDGE,"E104"),sQuery(id+"F0.wireOp",EDGE,"E105"),sQuery(id+"F0.wireOp",EDGE,"E106"),sQuery(id+"F0.wireOp",EDGE,"E118"),sQuery(id+"F0.wireOp",EDGE,"E119"),sQuery(id+"F0.wireOp",EDGE,"E120"),sQuery(id+"F0.wireOp",EDGE,"E128.MirrorCS"),sQuery(id+"F0.wireOp",EDGE,"E129.MirrorCS"),sQuery(id+"F0.wireOp",EDGE,"E133.MirrorCS")])]});
            transform(context, id + "F27", {"entities" : qUnion([Q0]), "transformType" : TransformType.TRANSLATION_3D, "dx" : 0 * mm, "dy" : 0 * mm, "dz" : 91.44 * mm, "makeCopy" : false});
        }
    });
